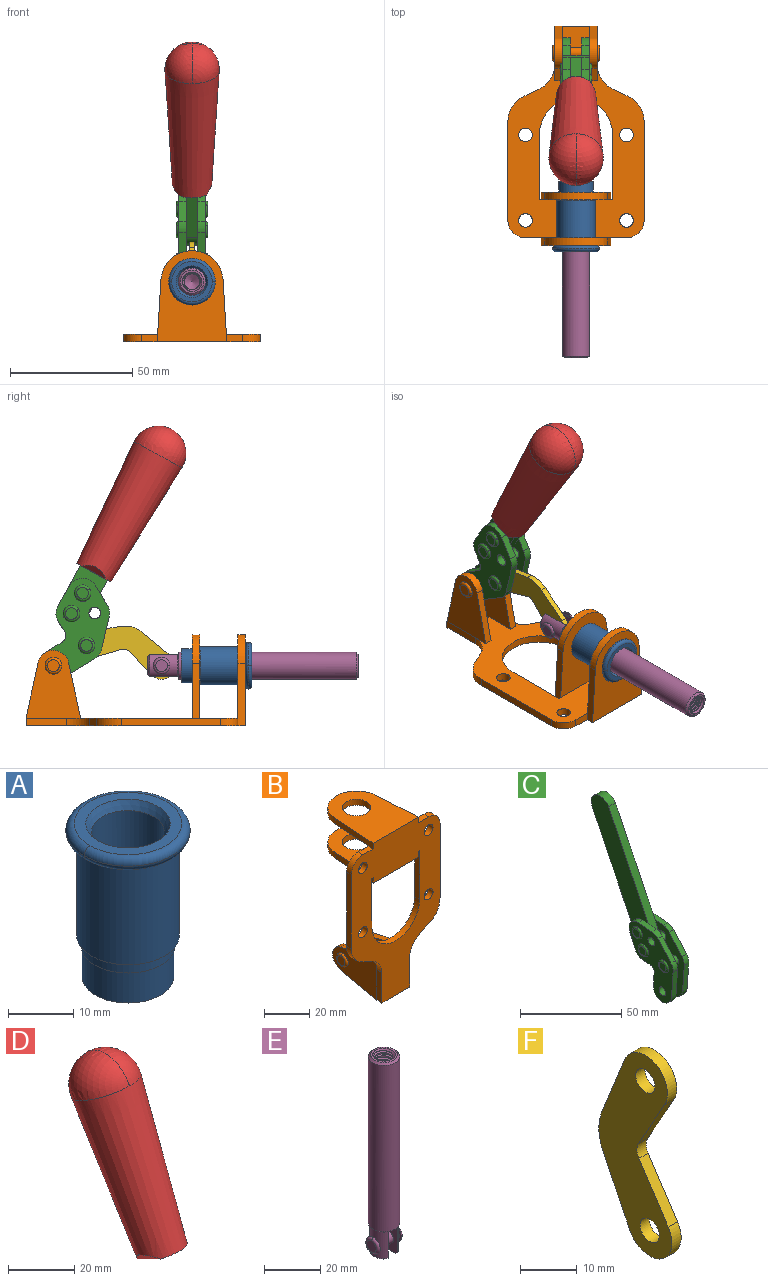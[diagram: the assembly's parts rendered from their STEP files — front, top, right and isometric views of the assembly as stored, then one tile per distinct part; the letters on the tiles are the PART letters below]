
ASSEMBLY  parts=6 mates=6
PART A: 15 faces, bbox 20.6x20.6x28.7 mm
  f0: torus R=8.26mm, axis (0,0,1), area 56.8mm2, adj f1,f10,f12
  f1: torus R=8.26mm, axis (0,0,1), area 56.8mm2, adj f0,f6,f13
  f2: cylinder r=5.59mm len=25.91mm, axis (0,0,1), area 909.6mm2, adj f3,f4
  f3: cone r=6.86mm half-angle=45deg, axis (0,0,-1), area 70.2mm2, adj f2,f14
  f4: cone r=6.47mm half-angle=30deg, axis (0,0,1), area 66.7mm2, adj f2,f13
  f5: cylinder r=7.04mm len=14.07mm, axis (0,0,1), area 252.6mm2, adj f11,f14
  f6: torus R=8.26mm, axis (0,0,1), area 56.8mm2, adj f1,f12,f13
  f7: cylinder r=7.16mm len=14.33mm, axis (0,0,1), area 91.5mm2, adj f9,f11
  f8: cylinder r=7.86mm len=18.42mm, axis (0,0,1), area 909.6mm2, adj f9,f10
  f9: plane 15.72x15.72mm, normal (0,0,-1), area 33mm2, adj f7,f8
  f10: plane 16.51x16.51mm, normal (0,0,-1), area 19.9mm2, adj f0,f8,f12
  f11: plane 14.33x14.33mm, normal (0,0,-1), area 5.7mm2, adj f5,f7
  f12: torus R=8.26mm, axis (0,0,1), area 56.8mm2, adj f0,f6,f10
  f13: plane 16.51x16.51mm, normal (0,0,1), area 82.7mm2, adj f1,f4,f6
  f14: plane 14.07x14.07mm, normal (0,0,-1), area 7.8mm2, adj f3,f5
PART B: 55 faces, bbox 55.7x37.4x89.8 mm
  f0: torus R=2.41mm, axis (-1,0,0), area 15mm2, adj f11,f15,f25
  f1: torus R=2.41mm, axis (-1,0,0), area 15mm2, adj f10,f12,f22
  f2: cylinder r=2.78mm len=5.56mm, axis (0,-1,0), area 54.2mm2, adj f30,f54
  f3: cylinder r=14.99mm len=29.97mm, axis (0,-1,0), area 145.9mm2, adj f30,f49,f53,f54
  f4: cylinder r=2.78mm len=5.56mm, axis (0,-1,0), area 54.2mm2, adj f30,f54
  f5: cylinder r=2.78mm len=5.56mm, axis (0,-1,0), area 54.2mm2, adj f30,f54
  f6: cylinder r=2.78mm len=5.56mm, axis (0,-1,0), area 54.2mm2, adj f30,f54
  f7: cylinder r=6.35mm len=12.7mm, axis (0,0,1), area 123.6mm2, adj f27,f51
  f8: cylinder r=6.35mm len=12.7mm, axis (0,0,-1), area 124.7mm2, adj f21,f35
  f9: cylinder r=2.41mm len=11.18mm, axis (-1,0,0), area 169.4mm2, adj f16,f19
  f10: plane 4.83x4.83mm, normal (1,0,0), area 18.3mm2, adj f1,f12
  f11: plane 4.83x4.83mm, normal (-1,0,0), area 18.3mm2, adj f0,f15
  f12: torus R=2.41mm, axis (-1,0,0), area 15mm2, adj f1,f10,f22
  f13: cylinder r=6.35mm len=12.41mm, axis (1,0,0), area 53.4mm2, adj f18,f19,f22,f23
  f14: cylinder r=6.35mm len=12.41mm, axis (-1,0,0), area 53.4mm2, adj f16,f17,f24,f25
  f15: torus R=2.41mm, axis (-1,0,0), area 15mm2, adj f0,f11,f25
  f16: plane 27.86x22.35mm, normal (1,0,0), area 425.4mm2, adj f9,f14,f17,f24,f30
  f17: plane 22.86x4.97mm, normal (0,0.21,0.98), area 72.5mm2, adj f14,f16,f25,f30
  f18: plane 22.86x4.97mm, normal (0,0.21,0.98), area 72.5mm2, adj f13,f19,f22,f30
  f19: plane 27.86x22.35mm, normal (-1,0,0), area 425.4mm2, adj f9,f13,f18,f23,f30
  f20: cylinder r=12.7mm len=25.35mm, axis (0,0,-1), area 119.8mm2, adj f21,f34,f35,f36
  f21: plane 34.21x28.07mm, normal (0,0,-1), area 702.4mm2, adj f8,f20,f30,f34,f36
  f22: plane 27.96x22.45mm, normal (1,0,0), area 407.2mm2, adj f1,f12,f13,f18,f23,f30,f42,f43
  f23: plane 22.86x4.97mm, normal (0,0.21,-0.98), area 72.5mm2, adj f13,f19,f22,f44
  f24: plane 22.86x4.97mm, normal (0,0.21,-0.98), area 72.5mm2, adj f14,f16,f25,f44
  f25: plane 27.86x22.35mm, normal (-1,0,0), area 407.1mm2, adj f0,f14,f15,f17,f24,f30,f45,f46
  f26: plane 3.1x0.95mm, normal (0,0,-1), area 2.7mm2, adj f30,f49,f50,f54
  f27: plane 34.21x28.07mm, normal (0,0,1), area 702.4mm2, adj f7,f28,f30,f50,f52
  f28: cylinder r=12.7mm len=25.35mm, axis (0,0,1), area 118.8mm2, adj f27,f50,f51,f52
  f29: plane 3.1x0.95mm, normal (0,0,-1), area 2.7mm2, adj f30,f52,f53,f54
  f30: plane 86.54x55.63mm, normal (0,1,0), area 2362.9mm2, adj f2,f3,f4,f5,f6,f16,f17,f18
  f31: plane 40.56x3.1mm, normal (-1,0,0), area 125.7mm2, adj f30,f32,f48,f54
  f32: cylinder r=7.11mm len=7.11mm, axis (0,-1,0), area 34.6mm2, adj f30,f31,f33,f54
  f33: plane 6.67x3.1mm, normal (0,0,1), area 20.4mm2, adj f30,f32,f34,f54
  f34: plane 25.39x3.13mm, normal (-1,0.06,0), area 79.5mm2, adj f20,f21,f33,f35,f54
  f35: plane 37.31x28.45mm, normal (0,0,1), area 789.9mm2, adj f8,f20,f34,f36,f54
  f36: plane 25.39x3.13mm, normal (1,0.06,0), area 79.5mm2, adj f20,f21,f35,f37,f54
  f37: plane 6.67x3.1mm, normal (0,0,1), area 20.4mm2, adj f30,f36,f38,f54
  f38: cylinder r=7.11mm len=7.11mm, axis (0,-1,0), area 34.6mm2, adj f30,f37,f39,f54
  f39: plane 40.56x3.1mm, normal (1,0,0), area 125.7mm2, adj f30,f38,f40,f54
  f40: cylinder r=11.18mm len=10.16mm, axis (0,-1,0), area 39.5mm2, adj f30,f39,f41,f54
  f41: plane 6.09x3.1mm, normal (0.42,0,-0.91), area 20.8mm2, adj f30,f40,f42,f54
  f42: cylinder r=11.18mm len=9.41mm, axis (0,-1,0), area 37.2mm2, adj f22,f30,f41,f43,f54
  f43: plane 16.5x3.1mm, normal (1,0,0), area 51.1mm2, adj f22,f42,f44,f54
  f44: plane 17.37x3.1mm, normal (0,0,-1), area 53.8mm2, adj f23,f24,f30,f43,f45,f54
  f45: plane 16.5x3.1mm, normal (-1,0,0), area 51.1mm2, adj f25,f44,f46,f54
  f46: cylinder r=11.18mm len=9.41mm, axis (0,-1,0), area 37.2mm2, adj f25,f30,f45,f47,f54
  f47: plane 6.09x3.1mm, normal (-0.42,0,-0.91), area 20.8mm2, adj f30,f46,f48,f54
  f48: cylinder r=11.18mm len=10.16mm, axis (0,-1,0), area 39.5mm2, adj f30,f31,f47,f54
  f49: plane 26.54x3.1mm, normal (-1,0,0), area 82.3mm2, adj f3,f26,f30,f54
  f50: plane 25.39x3.1mm, normal (1,0.06,0), area 78.8mm2, adj f26,f27,f28,f51,f54
  f51: plane 37.31x28.45mm, normal (0,0,-1), area 789.9mm2, adj f7,f28,f50,f52,f54
  f52: plane 25.39x3.1mm, normal (-1,0.06,0), area 78.8mm2, adj f27,f28,f29,f51,f54
  f53: plane 26.54x3.1mm, normal (1,0,0), area 82.3mm2, adj f3,f29,f30,f54
  f54: plane 89.66x55.63mm, normal (0,-1,0), area 2678.5mm2, adj f2,f3,f4,f5,f6,f26,f29,f31
PART C: 59 faces, bbox 12.9x60.2x99.6 mm
  f0: torus R=2.39mm, axis (-1,0,0), area 14.9mm2, adj f20,f43,f51
  f1: torus R=2.39mm, axis (-1,0,0), area 14.9mm2, adj f19,f42,f51
  f2: torus R=2.39mm, axis (-1,0,0), area 14.9mm2, adj f18,f35,f51
  f3: torus R=2.39mm, axis (-1,0,0), area 14.9mm2, adj f14,f17,f23
  f4: torus R=2.39mm, axis (-1,0,0), area 14.9mm2, adj f13,f16,f23
  f5: torus R=2.39mm, axis (-1,0,0), area 14.9mm2, adj f12,f15,f23
  f6: cylinder r=2.39mm len=4.78mm, axis (1,0,0), area 46.5mm2, adj f48,f50,f51
  f7: cylinder r=2.39mm len=4.78mm, axis (1,0,0), area 46.5mm2, adj f50,f51
  f8: cylinder r=6.35mm len=12.68mm, axis (1,0,0), area 61.8mm2, adj f38,f39,f50,f51
  f9: cylinder r=2.39mm len=4.78mm, axis (-1,0,0), area 70.5mm2, adj f46,f50
  f10: cylinder r=2.39mm len=4.78mm, axis (-1,0,0), area 46.5mm2, adj f23,f45,f46
  f11: cylinder r=2.39mm len=4.78mm, axis (-1,0,0), area 46.5mm2, adj f23,f46
  f12: plane 4.78x4.78mm, normal (1,0,0), area 17.9mm2, adj f5,f15
  f13: plane 4.78x4.78mm, normal (1,0,0), area 17.9mm2, adj f4,f16
  f14: plane 4.78x4.78mm, normal (1,0,0), area 17.9mm2, adj f3,f17
  f15: torus R=2.39mm, axis (-1,0,0), area 14.9mm2, adj f5,f12,f23
  f16: torus R=2.39mm, axis (-1,0,0), area 14.9mm2, adj f4,f13,f23
  f17: torus R=2.39mm, axis (-1,0,0), area 14.9mm2, adj f3,f14,f23
  f18: plane 4.78x4.78mm, normal (-1,0,0), area 17.9mm2, adj f2,f35
  f19: plane 4.78x4.78mm, normal (-1,0,0), area 17.9mm2, adj f1,f42
  f20: plane 4.78x4.78mm, normal (-1,0,0), area 17.9mm2, adj f0,f43
  f21: plane 2.26x0.2mm, normal (1,0,0), area 0.2mm2, adj f31,f44
  f22: plane 2.26x0.2mm, normal (-1,0,0), area 0.2mm2, adj f41,f44
  f23: plane 39.37x30.77mm, normal (1,0,0), area 565.5mm2, adj f3,f4,f5,f10,f11,f15,f16,f17
  f24: cylinder r=6.1mm len=4.15mm, axis (-1,0,0), area 14.7mm2, adj f23,f25,f32,f46
  f25: plane 10.25x9.01mm, normal (0,-0.75,0.66), area 42.3mm2, adj f23,f24,f26,f46
  f26: cylinder r=6.35mm len=4.64mm, axis (-1,0,0), area 15.6mm2, adj f23,f25,f27,f46
  f27: plane 15.84x3.1mm, normal (0,-1,-0.07), area 49.2mm2, adj f23,f26,f28,f46
  f28: cylinder r=6.35mm len=12.68mm, axis (-1,0,0), area 61.8mm2, adj f23,f27,f29,f46
  f29: plane 8.11x3.1mm, normal (0,1,0.07), area 25.2mm2, adj f23,f28,f30,f46
  f30: cylinder r=3.05mm len=3.25mm, axis (-1,0,0), area 14.8mm2, adj f23,f29,f31,f46
  f31: plane 5.99x3.1mm, normal (0,0.07,-1), area 18.6mm2, adj f21,f23,f30,f44,f46
  f32: plane 9.5x3.1mm, normal (0,-0.07,1), area 29.5mm2, adj f23,f24,f33,f46,f47
  f33: cylinder r=6.1mm len=8.63mm, axis (-1,0,0), area 39.1mm2, adj f23,f32,f34,f47
  f34: plane 8.65x3.96mm, normal (0,0.91,-0.42), area 29.5mm2, adj f23,f33,f44,f47
  f35: torus R=2.39mm, axis (-1,0,0), area 14.9mm2, adj f2,f18,f51
  f36: plane 10.25x9.01mm, normal (0,-0.75,0.66), area 42.3mm2, adj f37,f49,f50,f51
  f37: cylinder r=6.35mm len=4.64mm, axis (1,0,0), area 15.6mm2, adj f36,f38,f50,f51
  f38: plane 15.84x3.1mm, normal (0,-1,-0.07), area 49.2mm2, adj f8,f37,f50,f51
  f39: plane 8.11x3.1mm, normal (0,1,0.07), area 25.2mm2, adj f8,f40,f50,f51
  f40: cylinder r=3.05mm len=3.25mm, axis (1,0,0), area 14.8mm2, adj f39,f41,f50,f51
  f41: plane 5.99x3.1mm, normal (0,0.07,-1), area 18.6mm2, adj f22,f40,f44,f50,f51
  f42: torus R=2.39mm, axis (-1,0,0), area 14.9mm2, adj f1,f19,f51
  f43: torus R=2.39mm, axis (-1,0,0), area 14.9mm2, adj f0,f20,f51
  f44: cylinder r=6.35mm len=12.12mm, axis (-1,0,0), area 128.9mm2, adj f21,f22,f23,f31,f34,f41,f46,f47
  f45: plane 2.65x1.35mm, normal (1,0,0), area 1mm2, adj f10,f55
  f46: plane 39.08x20.42mm, normal (-1,0,0), area 412.5mm2, adj f9,f10,f11,f24,f25,f26,f27,f28
  f47: plane 77.62x39.82mm, normal (1,0,0), area 850mm2, adj f32,f33,f34,f44,f53,f54,f55
  f48: plane 2.65x1.35mm, normal (-1,0,0), area 1mm2, adj f6,f55
  f49: cylinder r=6.1mm len=4.15mm, axis (1,0,0), area 14.7mm2, adj f36,f50,f51,f56
  f50: plane 39.08x20.42mm, normal (1,0,0), area 412.5mm2, adj f6,f7,f8,f9,f36,f37,f38,f39
  f51: plane 39.37x30.77mm, normal (-1,0,0), area 565.5mm2, adj f0,f1,f2,f6,f7,f8,f35,f36
  f52: plane 8.65x3.96mm, normal (0,0.91,-0.42), area 29.5mm2, adj f44,f51,f57,f58
  f53: plane 68.49x33.4mm, normal (0,0.9,-0.44), area 358.1mm2, adj f44,f47,f54,f58
  f54: cylinder r=6.35mm len=12.06mm, axis (1,0,0), area 93.7mm2, adj f47,f53,f55,f58
  f55: plane 68.49x33.4mm, normal (0,-0.9,0.44), area 358.1mm2, adj f44,f45,f46,f47,f48,f50,f54,f58
  f56: plane 9.5x3.1mm, normal (0,-0.07,1), area 29.5mm2, adj f49,f50,f51,f57,f58
  f57: cylinder r=6.1mm len=8.63mm, axis (1,0,0), area 39.1mm2, adj f51,f52,f56,f58
  f58: plane 77.62x39.82mm, normal (-1,0,0), area 850mm2, adj f44,f52,f53,f54,f55,f56,f57
PART D: 11 faces, bbox 22.3x42.6x64.5 mm
  f0: sphere r=11.13mm, area 411.4mm2, adj f1,f8
  f1: cone r=11.11mm half-angle=3.3deg, axis (0,0.44,0.9), area 3251.8mm2, adj f0,f7,f8,f9,f10
  f2: cylinder r=6.16mm len=11.7mm, axis (1,0,0), area 89.5mm2, adj f3,f4,f5,f6
  f3: plane 60.23x36.75mm, normal (-1,0,0), area 763.6mm2, adj f2,f4,f6,f10
  f4: plane 51.37x25.05mm, normal (0,0.9,-0.44), area 264.2mm2, adj f2,f3,f5,f10
  f5: plane 60.23x36.75mm, normal (1,0,0), area 763.6mm2, adj f2,f4,f6,f10
  f6: plane 51.37x25.05mm, normal (0,-0.9,0.44), area 264.2mm2, adj f2,f3,f5,f10
  f7: plane 9.95x5.95mm, normal (0.71,-0.31,-0.64), area 25.8mm2, adj f1,f10
  f8: sphere r=11.13mm, area 411.4mm2, adj f0,f1
  f9: plane 9.95x5.95mm, normal (-0.71,-0.31,-0.64), area 25.8mm2, adj f1,f10
  f10: plane 14.27x11.38mm, normal (0,-0.44,-0.9), area 106.7mm2, adj f1,f3,f4,f5,f6,f7,f9
PART E: 48 faces, bbox 12.6x11.1x86.1 mm
  f0: torus R=2.41mm, axis (-1,0,0), area 15mm2, adj f30,f32,f34
  f1: torus R=2.41mm, axis (-1,0,0), area 15mm2, adj f29,f31,f33
  f2: cylinder r=5.54mm len=72.39mm, axis (0,0,1), area 2518.5mm2, adj f3,f4,f42,f43
  f3: cone r=5.54mm half-angle=45deg, axis (0,0,1), area 7.6mm2, adj f2,f5,f41
  f4: cone r=5.54mm half-angle=45deg, axis (0,0,-1), area 34.9mm2, adj f2,f39
  f5: cylinder r=5.08mm len=11.48mm, axis (0,0,1), area 108.3mm2, adj f3,f7,f8,f41
  f6: cylinder r=2.41mm len=4.83mm, axis (-1,0,0), area 71.2mm2, adj f40,f41
  f7: cylinder r=2.41mm len=4.83mm, axis (-1,0,0), area 7.6mm2, adj f5,f34
  f8: cone r=5.08mm half-angle=45deg, axis (0,0,1), area 10.6mm2, adj f5,f37,f41
  f9: cone r=3.98mm half-angle=45deg, axis (0,0,1), area 17.6mm2, adj f27,f39,f45,f46,f47
  f10: cylinder r=2.41mm len=4.83mm, axis (-1,0,0), area 7.6mm2, adj f33,f38
  f11: cylinder r=3.2mm len=6.4mm, axis (0,0,1), area 78.4mm2, adj f12,f28,f44,f45,f47
  f12: cylinder r=3.2mm len=6.4mm, axis (0,0,1), area 10.5mm2, adj f11,f13,f45,f47
  f13: cylinder r=3.2mm len=6.4mm, axis (0,0,1), area 10.5mm2, adj f12,f14,f45,f47
  f14: cylinder r=3.2mm len=6.4mm, axis (0,0,1), area 10.5mm2, adj f13,f15,f45,f47
  f15: cylinder r=3.2mm len=6.4mm, axis (0,0,1), area 10.5mm2, adj f14,f16,f45,f47
  f16: cylinder r=3.2mm len=6.4mm, axis (0,0,1), area 10.5mm2, adj f15,f17,f45,f47
  f17: cylinder r=3.2mm len=6.4mm, axis (0,0,1), area 10.5mm2, adj f16,f18,f45,f47
  f18: cylinder r=3.2mm len=6.4mm, axis (0,0,1), area 10.5mm2, adj f17,f19,f45,f47
  f19: cylinder r=3.2mm len=6.4mm, axis (0,0,1), area 10.5mm2, adj f18,f20,f45,f47
  f20: cylinder r=3.2mm len=6.4mm, axis (0,0,1), area 10.5mm2, adj f19,f21,f45,f47
  f21: cylinder r=3.2mm len=6.4mm, axis (0,0,1), area 10.5mm2, adj f20,f22,f45,f47
  f22: cylinder r=3.2mm len=6.4mm, axis (0,0,1), area 10.5mm2, adj f21,f23,f45,f47
  f23: cylinder r=3.2mm len=6.4mm, axis (0,0,1), area 10.5mm2, adj f22,f24,f45,f47
  f24: cylinder r=3.2mm len=6.4mm, axis (0,0,1), area 10.5mm2, adj f23,f25,f45,f47
  f25: cylinder r=3.2mm len=6.4mm, axis (0,0,1), area 10.5mm2, adj f24,f26,f45,f47
  f26: cylinder r=3.2mm len=6.4mm, axis (0,0,1), area 10.5mm2, adj f25,f27,f45,f47
  f27: cylinder r=3.2mm len=6.4mm, axis (0,0,1), area 7.4mm2, adj f9,f26,f45,f47
  f28: cone r=3.2mm half-angle=60deg, axis (0,0,1), area 37.2mm2, adj f11
  f29: plane 4.83x4.83mm, normal (-1,0,0), area 18.3mm2, adj f1,f31
  f30: plane 4.83x4.83mm, normal (1,0,0), area 18.3mm2, adj f0,f32
  f31: torus R=2.41mm, axis (-1,0,0), area 15mm2, adj f1,f29,f33
  f32: torus R=2.41mm, axis (-1,0,0), area 15mm2, adj f0,f30,f34
  f33: plane 6.83x6.83mm, normal (1,0,0), area 18.3mm2, adj f1,f10,f31
  f34: plane 6.83x6.83mm, normal (-1,0,0), area 18.3mm2, adj f0,f7,f32
  f35: cone r=5.08mm half-angle=45deg, axis (0,0,1), area 10.6mm2, adj f36,f38,f40
  f36: plane 7.25x1.97mm, normal (0,0,-1), area 10mm2, adj f35,f40
  f37: plane 7.25x1.97mm, normal (0,0,-1), area 10mm2, adj f8,f41
  f38: cylinder r=5.08mm len=11.48mm, axis (0,0,1), area 108.3mm2, adj f10,f35,f40,f42
  f39: plane 9.55x9.55mm, normal (0,0,1), area 22mm2, adj f4,f9
  f40: plane 12.76x10.09mm, normal (1,0,0), area 95.7mm2, adj f6,f35,f36,f38,f42,f43
  f41: plane 12.76x10.09mm, normal (-1,0,0), area 95.7mm2, adj f3,f5,f6,f8,f37,f43
  f42: cone r=5.54mm half-angle=45deg, axis (0,0,1), area 7.6mm2, adj f2,f38,f40
  f43: plane 11.07x4.7mm, normal (0,0,-1), area 50.4mm2, adj f2,f40,f41
  f44: plane 0.89x0.62mm, normal (-1,0,0), area 0.3mm2, adj f11,f45,f46,f47
  f45: bspline ~24.8x7.63mm, area 266.6mm2, adj f9,f11,f12,f13,f14,f15,f16,f17
  f46: bspline ~24.87x7.63mm, area 73.6mm2, adj f9,f44,f45,f47
  f47: bspline ~24.98x7.63mm, area 272.5mm2, adj f9,f11,f12,f13,f14,f15,f16,f17
PART F: 12 faces, bbox 2.3x18.2x42.8 mm
  f0: cylinder r=2.4mm len=4.8mm, axis (1,0,0), area 34.9mm2, adj f4,f11
  f1: cylinder r=10.41mm len=8.47mm, axis (1,0,0), area 20.2mm2, adj f4,f9,f10,f11
  f2: cylinder r=3.05mm len=3.16mm, axis (1,0,0), area 7.7mm2, adj f4,f6,f7,f11
  f3: cylinder r=2.4mm len=4.8mm, axis (1,0,0), area 34.9mm2, adj f4,f11
  f4: plane 42.81x18.23mm, normal (-1,0,0), area 414.1mm2, adj f0,f1,f2,f3,f5,f6,f7,f8
  f5: cylinder r=5.54mm len=10.67mm, axis (1,0,0), area 41.8mm2, adj f4,f6,f10,f11
  f6: plane 11.66x6.53mm, normal (0,-0.87,-0.49), area 30.9mm2, adj f2,f4,f5,f11
  f7: plane 11.17x7.33mm, normal (0,-0.84,0.55), area 30.9mm2, adj f2,f4,f8,f11
  f8: cylinder r=5.54mm len=10.51mm, axis (1,0,0), area 41.8mm2, adj f4,f7,f9,f11
  f9: plane 13.67x6.67mm, normal (0,0.9,-0.44), area 35.1mm2, adj f1,f4,f8,f11
  f10: plane 14.1x5.7mm, normal (0,0.93,0.37), area 35.1mm2, adj f1,f4,f5,f11
  f11: plane 42.81x18.23mm, normal (1,0,0), area 414.1mm2, adj f0,f1,f2,f3,f5,f6,f7,f8
PLACE A rot(axis=(1,0,0),90deg) t=(0,9.14,0)mm
PLACE B rot(axis=(1,0,0),90deg) t=(0,9.14,0)mm fixed
PLACE C rot(axis=(1,0,0),54.5deg) t=(0,0.81,23.18)mm
PLACE D rot(axis=(1,0,0),54.5deg) t=(0.04,0.81,23.18)mm
PLACE E rot(axis=(1,0,0),90deg) t=(0,12.52,0)mm
PLACE F rot(axis=(1,0,0),107.1deg) t=(0,19.08,5.65)mm
MATE fastened B.f7 <-> A.f0  axis (0,-1,0) through (0,-37.25,24.61)mm
MATE revolute C.f7 <-> B.f0  axis (-1,0,0) through (0,41.23,24.61)mm
MATE fastened D.f2 <-> C.f54  axis (-1,0,0) through (2.35,-2.58,112.82)mm
MATE slider E.f2 <-> B.f7  axis (0,-1,0) through (0,-46.27,24.61)mm
MATE revolute C.f4 <-> F.f3  axis (-1,0,0) through (0,27.69,32.9)mm
MATE revolute F.f5 <-> E.f6  axis (1,0,0) through (0,-2.96,24.61)mm
